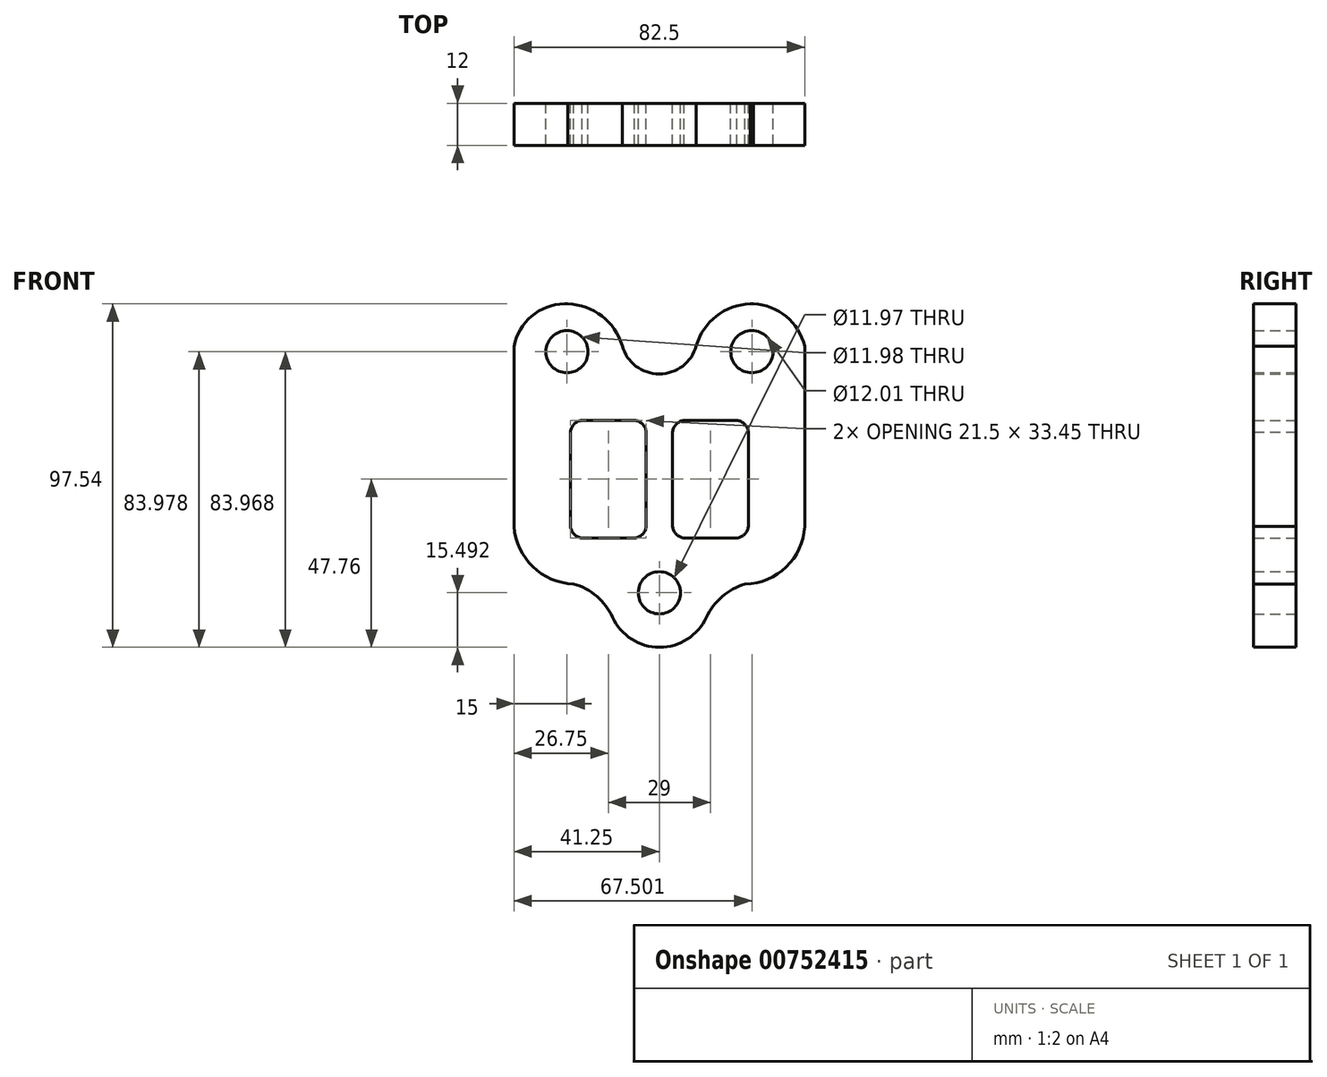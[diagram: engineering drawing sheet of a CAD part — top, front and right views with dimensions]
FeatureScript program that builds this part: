
annotation { "Feature Type Name" : "Feature", "Feature Type Description" : "" }
export const myFeature = defineFeature(function(context is Context, id is Id, definition is map)
    precondition{}
    {
        {
            var Q0;
            Q0=qCreatedBy(makeId("Front.planeOp"),FACE);
            var sketch = newSketch(context, id + "F0", { "sketchPlane" : qUnion([Q0])});
            skLineSegment(sketch, "E0.bottom", {"start": v(-41.25, 48.77) * mm, "end": v(41.25, 48.77) * mm});
            skLineSegment(sketch, "E0.top", {"start": v(-41.25, -48.77) * mm, "end": v(41.25, -48.77) * mm});
            skLineSegment(sketch, "E0.left", {"start": v(-41.25, 48.77) * mm, "end": v(-41.25, -48.77) * mm});
            skLineSegment(sketch, "E0.right", {"start": v(41.25, 48.77) * mm, "end": v(41.25, -48.77) * mm});
            skPoint(sketch, "E0.middle", {"position": v(0, 0) * mm});
            skLineSegment(sketch, "E1.bottom", {"start": v(-25.25, -17.73) * mm, "end": v(-3.75, -17.73) * mm});
            skLineSegment(sketch, "E1.top", {"start": v(-25.25, 15.72) * mm, "end": v(-3.75, 15.72) * mm});
            skLineSegment(sketch, "E1.left", {"start": v(-25.25, -17.73) * mm, "end": v(-25.25, 15.72) * mm});
            skLineSegment(sketch, "E1.right", {"start": v(-3.75, -17.73) * mm, "end": v(-3.75, 15.72) * mm});
            skLineSegment(sketch, "E2.bottom", {"start": v(3.75, -17.73) * mm, "end": v(25.25, -17.73) * mm});
            skLineSegment(sketch, "E2.top", {"start": v(3.75, 15.72) * mm, "end": v(25.25, 15.72) * mm});
            skLineSegment(sketch, "E2.left", {"start": v(3.75, -17.73) * mm, "end": v(3.75, 15.72) * mm});
            skLineSegment(sketch, "E2.right", {"start": v(25.25, -17.73) * mm, "end": v(25.25, 15.72) * mm});
            skCircle(sketch, "E3", {"center": v(-26.25, 35.22) * mm, "radius": 6 * mm});
            skCircle(sketch, "E4", {"center": v(26.25, 35.22) * mm, "radius": 6 * mm});
            skCircle(sketch, "E5", {"center": v(0, -33.28) * mm, "radius": 6 * mm});
            skSolve(sketch);
        }
        {
            var Q0;
            Q0=makeQuery(id+"F0.imprint","IMPRINT",FACE,{"disambiguationData":[TD([[makeQuery(id+"F0.imprint","IMPRINT",EDGE,{"derivedFrom":sQuery(id+"F0.wireOp",EDGE,"E0.bottom")}),-1.0]])]});
            var sketch = newSketch(context, id + "F1", { "sketchPlane" : qUnion([Q0])});
            skArc(sketch, "E6", {"start": v(-26.69, 48.77) * mm, "mid": v(-36.34, 45.2) * mm, "end": v(-41.25, 36.17) * mm});
            skArc(sketch, "E7", {"start": v(41.25, 36.17) * mm, "mid": v(36.2, 45.04) * mm, "end": v(26.69, 48.77) * mm});
            skSolve(sketch);
        }
        {
            var Q0;
            {var subQ5=sQuery(id+"F1.wireOp",EDGE,"E7");Q0=makeQuery(id+"F1.imprint","IMPRINT",FACE,{"disambiguationData":[TD([[makeQuery(id+"F1.imprint","IMPRINT",EDGE,{"derivedFrom":subQ5}),1.0]])]});}
            var sketch = newSketch(context, id + "F2", { "sketchPlane" : qUnion([Q0])});
            skArc(sketch, "E8", {"start": v(-10.48, 36.85) * mm, "mid": v(-16.56, 45.52) * mm, "end": v(-26.64, 48.77) * mm});
            skArc(sketch, "E9", {"start": v(27, 48.77) * mm, "mid": v(16.67, 45.67) * mm, "end": v(10.48, 36.85) * mm});
            skArc(sketch, "E10", {"start": v(-10.48, 36.85) * mm, "mid": v(0, 28.9) * mm, "end": v(10.48, 36.85) * mm});
            skSolve(sketch);
        }
        {
            var Q0;
            {var subQ16=sQuery(id+"F2.wireOp",EDGE,"E10");Q0=makeQuery(id+"F2.imprint","IMPRINT",FACE,{"disambiguationData":[TD([[makeQuery(id+"F2.imprint","IMPRINT",EDGE,{"derivedFrom":subQ16}),-1.0]])]});}
            var sketch = newSketch(context, id + "F3", { "sketchPlane" : qUnion([Q0])});
            skArc(sketch, "E11", {"start": v(-13.14, -40.5) * mm, "mid": v(0, -48.76) * mm, "end": v(13.14, -40.5) * mm});
            skArc(sketch, "E12", {"start": v(24.34, -30.82) * mm, "mid": v(35.87, -25.92) * mm, "end": v(41.25, -14.6) * mm});
            skArc(sketch, "E13", {"start": v(-41.25, -14.6) * mm, "mid": v(-35.87, -25.92) * mm, "end": v(-24.34, -30.82) * mm});
            skArc(sketch, "E14", {"start": v(24.34, -30.82) * mm, "mid": v(17.68, -34.43) * mm, "end": v(13.14, -40.5) * mm});
            skArc(sketch, "E15", {"start": v(-13.14, -40.5) * mm, "mid": v(-17.68, -34.43) * mm, "end": v(-24.34, -30.82) * mm});
            skSolve(sketch);
        }
        {
            var Q0;
            Q0=makeQuery(id+"F1.imprint","IMPRINT",FACE,{"disambiguationData":[TD([[makeQuery(id+"F1.imprint","IMPRINT",EDGE,{"derivedFrom":makeQuery(id+"F0.imprint","IMPRINT",EDGE,{"derivedFrom":sQuery(id+"F0.wireOp",EDGE,"E1.bottom")})}),1.0]])]});
            var sketch = newSketch(context, id + "F4", { "sketchPlane" : qUnion([Q0])});
            skArc(sketch, "E16", {"start": v(-21.95, 15.72) * mm, "mid": v(-24.19, 14.65) * mm, "end": v(-25.25, 12.42) * mm});
            skArc(sketch, "E17", {"start": v(-3.75, 12.42) * mm, "mid": v(-4.81, 14.65) * mm, "end": v(-7.05, 15.72) * mm});
            skArc(sketch, "E18", {"start": v(-25.25, -14.43) * mm, "mid": v(-24.19, -16.67) * mm, "end": v(-21.95, -17.73) * mm});
            skArc(sketch, "E19", {"start": v(-7.05, -17.73) * mm, "mid": v(-4.81, -16.67) * mm, "end": v(-3.75, -14.43) * mm});
            skArc(sketch, "E20", {"start": v(7.05, 15.72) * mm, "mid": v(4.81, 14.65) * mm, "end": v(3.75, 12.42) * mm});
            skArc(sketch, "E21", {"start": v(3.75, -14.43) * mm, "mid": v(4.81, -16.67) * mm, "end": v(7.05, -17.73) * mm});
            skArc(sketch, "E22", {"start": v(25.25, 12.42) * mm, "mid": v(24.19, 14.65) * mm, "end": v(21.95, 15.72) * mm});
            skArc(sketch, "E23", {"start": v(21.95, -17.73) * mm, "mid": v(24.19, -16.67) * mm, "end": v(25.25, -14.43) * mm});
            skLineSegment(sketch, "E24", {"start": v(-25.25, -14.43) * mm, "end": v(-25.25, 12.42) * mm});
            skLineSegment(sketch, "E25", {"start": v(-21.95, 15.72) * mm, "end": v(-7.05, 15.72) * mm});
            skLineSegment(sketch, "E26", {"start": v(7.05, 15.72) * mm, "end": v(21.95, 15.72) * mm});
            skLineSegment(sketch, "E27", {"start": v(7.05, -17.73) * mm, "end": v(21.95, -17.73) * mm});
            skLineSegment(sketch, "E28", {"start": v(3.75, -14.43) * mm, "end": v(3.75, 12.42) * mm});
            skLineSegment(sketch, "E29", {"start": v(25.25, 12.42) * mm, "end": v(25.25, -14.43) * mm});
            skCircle(sketch, "E30", {"center": v(0, -33.28) * mm, "radius": 5.99 * mm});
            skLineSegment(sketch, "E31", {"start": v(-21.95, -17.73) * mm, "end": v(-7.05, -17.73) * mm});
            skLineSegment(sketch, "E32", {"start": v(-3.75, -14.43) * mm, "end": v(-3.75, 12.42) * mm});
            skCircle(sketch, "E33", {"center": v(-26.25, 35.2) * mm, "radius": 5.99 * mm});
            skCircle(sketch, "E34", {"center": v(26.25, 35.2) * mm, "radius": 6 * mm});
            skLineSegment(sketch, "E35.bottom", {"start": v(41.25, 48.77) * mm, "end": v(-41.25, 48.77) * mm});
            skLineSegment(sketch, "E35.top", {"start": v(41.25, -48.77) * mm, "end": v(-41.25, -48.77) * mm});
            skLineSegment(sketch, "E35.left", {"start": v(41.25, 48.77) * mm, "end": v(41.25, -48.77) * mm});
            skLineSegment(sketch, "E35.right", {"start": v(-41.25, 48.77) * mm, "end": v(-41.25, -48.77) * mm});
            skPoint(sketch, "E35.middle", {"position": v(0, 0) * mm});
            skArc(sketch, "E36", {"start": v(-13.28, -40.23) * mm, "mid": v(-17.76, -34.3) * mm, "end": v(-24.32, -30.76) * mm});
            skArc(sketch, "E37", {"start": v(-41.25, -14.43) * mm, "mid": v(-35.94, -25.87) * mm, "end": v(-24.32, -30.76) * mm});
            skArc(sketch, "E38", {"start": v(-13.28, -40.23) * mm, "mid": v(0.04, -48.77) * mm, "end": v(13.35, -40.23) * mm});
            skArc(sketch, "E39", {"start": v(24.34, -30.82) * mm, "mid": v(17.82, -34.32) * mm, "end": v(13.35, -40.23) * mm});
            skArc(sketch, "E40", {"start": v(24.34, -30.82) * mm, "mid": v(36.02, -25.93) * mm, "end": v(41.25, -14.4) * mm});
            skLineSegment(sketch, "E41", {"start": v(-41.25, 36.62) * mm, "end": v(-41.25, -14.43) * mm});
            skLineSegment(sketch, "E42", {"start": v(41.25, 36.75) * mm, "end": v(41.25, -14.4) * mm});
            skArc(sketch, "E43", {"start": v(41.25, 36.75) * mm, "mid": v(36.02, 45.2) * mm, "end": v(26.73, 48.77) * mm});
            skArc(sketch, "E44", {"start": v(26.73, 48.77) * mm, "mid": v(16.57, 45.61) * mm, "end": v(10.48, 36.89) * mm});
            skArc(sketch, "E45", {"start": v(-10.57, 36.89) * mm, "mid": v(-0.04, 28.86) * mm, "end": v(10.48, 36.89) * mm});
            skArc(sketch, "E46", {"start": v(-10.57, 36.89) * mm, "mid": v(-16.66, 45.59) * mm, "end": v(-26.79, 48.77) * mm});
            skArc(sketch, "E47", {"start": v(-26.79, 48.77) * mm, "mid": v(-36.25, 45.35) * mm, "end": v(-41.25, 36.62) * mm});
            skSolve(sketch);
        }
        {
            var Q0;
            {var subQ0=sQuery(id+"F4.wireOp",EDGE,"E19");Q0=makeQuery(id+"F4.imprint","IMPRINT",FACE,{"disambiguationData":[TD([[makeQuery(id+"F4.imprint","IMPRINT",EDGE,{"derivedFrom":subQ0}),-1.0]])]});}
            var Q1;
            {var subQ0=sQuery(id+"F4.wireOp",EDGE,"E18");Q1=makeQuery(id+"F4.imprint","IMPRINT",FACE,{"disambiguationData":[TD([[makeQuery(id+"F4.imprint","IMPRINT",EDGE,{"derivedFrom":subQ0}),-1.0]])]});}
            var Q2;
            {var subQ0=sQuery(id+"F4.wireOp",EDGE,"E16");Q2=makeQuery(id+"F4.imprint","IMPRINT",FACE,{"disambiguationData":[TD([[makeQuery(id+"F4.imprint","IMPRINT",EDGE,{"derivedFrom":subQ0}),-1.0]])]});}
            var Q3;
            {var subQ0=sQuery(id+"F4.wireOp",EDGE,"E17");Q3=makeQuery(id+"F4.imprint","IMPRINT",FACE,{"disambiguationData":[TD([[makeQuery(id+"F4.imprint","IMPRINT",EDGE,{"derivedFrom":subQ0}),-1.0]])]});}
            var Q4;
            Q4=makeQuery(id+"F4.imprint","IMPRINT",FACE,{"disambiguationData":[TD([[makeQuery(id+"F4.imprint","IMPRINT",EDGE,{"derivedFrom":sQuery(id+"F4.wireOp",EDGE,"E20")}),-1.0]])]});
            extrude(context, id + "F5", {"entities" : qUnion([Q0, Q1, Q2, Q3, Q4]), "depth" : 12 * mm, "offsetDistance" : 25 * mm});
        }
    });
